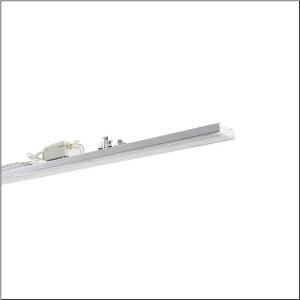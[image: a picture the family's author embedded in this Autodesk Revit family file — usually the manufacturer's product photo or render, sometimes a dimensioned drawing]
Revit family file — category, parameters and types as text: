
# Revit family: licross_11_recessed_ho_51tl18de465m
name_source: partatom
category: Lighting Fixtures
units: mm (PartAtom-declared; Revit-internal decimal feet)

## family parameters
Cut with Voids When Loaded = No
Host = Face
Light Source = No
Part Type = Normal
Room Calculation Point = No
Round Connector Dimension = Use Diameter
Shared = No

## types (1)
- --- (1 x LED, 6940 lm, 40.2 W, 4000K)
    Apparent Load = 40 VA
    CIE Flux Codes = 78 94 99 100 100
    Color Rendering = 80
    Color Temperature = 4000K
    Default Elevation = 1800 mm
    Description = Licross 11 Recessed HO, luminaire insert, of sheet steel, coil coated, white, length: 750mm, width: 66mm, height: 67mm, LED rated luminous flux: 6.940lm, light colour: 840, SDCM (Standard Deviation of Colour Matching)MacAdam ≤ 2 SDCM (initial), control gear: DALI 2, with plug, 5-pole, with phase selection, mains connection: 220..240V, AC, 50/60Hz, rated input power: 40W, internal wiring halogen-free, primary light control with lens, of plastic, primary optical cover: cover, of PMMA, light emission: direct distribution, primary light characteristic: symmetric, protection rating (complete): IP40, insulation class (complete): insulation class I (protective earthing), certification: CE, ENEC, VDE, UKCA, protection symbol: D if used in an environment without relevant dust loads with corresponding accessories, impact resistance: IK06, permissible ambient temperature for indoor applications: -25..+35°C, corresponds to IFS (International Featured Standards) requirements for safety and quality in the food industry, reducing of maximum allowable ambient temperature of 5°C with ceiling mounting, LABS conformity tested according to VDMA 24364:2018-05, The light source and the operating device comply with the requirements of the Ecodesign Regulation (EU) 2019/2020 and are replaceable in accordance with this regulation, packaging unit: 1 piece
    Height = 58 mm
    Lamp = 1 x LED
    Lamp Light Flux = 6940 lm
    Lamp Power = 40.2 W
    Lamp count = 1
    Length = 750 mm
    Luminous efficacy = 173 lm/W
    Manufacturer = Siteco
    ModVariant = No
    Model = 51TL18DE465M
    Mounting Place = Ceiling
    Mounting Type = Pendant
    Number of Poles = 1
    OnlyDefault = Yes
    Power Factor = 1
    Product Name = Licross 11 Recessed HO
    Product group = luminaire insert | ceiling pendant
    ProductGroupID = 901
    Protection Class = Protection class I
    Protection Degree = IP 40
    RLX_Detail_Level = 1
    RLX_Emergency_Light_Flux = 0 lm
    RLX_Emergency_Type = 0
    RLX_Emergency_Type_DB = No
    RlxData = <blob elided: 29489 chars, md5=54cdab48>
    Socket = socket
    Standby Power = 0 W
    System Light Flux = 6940 lm
    System Power = 40 W
    Type Comments = factory setting: luminous flux: 100 % | dim-lin: 254 | 522 mA
    Type Image = l_1296930.jpg
    URL = http://relux.com
    VarID = @adj_102333
    Voltage = 0 V
    Weight = 0.00 kg
    Width = 66 mm

## geometry (parser evidence)
native form markers: Blend x4, Sweep x9
no freeform markers — native parametric forms only
